# Revit family: Mailboxes_Aluminum-Standard_System-Salsbury_Industries-Wall_Installation
name_source: partatom
category: Specialty Equipment
revit_build: Autodesk Revit 2016 (Build: 20150714_1515(x64)
units: mm (PartAtom-declared; Revit-internal decimal feet)

## family parameters
Always vertical = Yes
Cut with Voids When Loaded = No
Host = Wall
OmniClass Number = 23.40.90.14.11
OmniClass Title = Mail Boxes
Part Type = Normal
Room Calculation Point = No
Round Connector Dimension = Use Diameter
Shared = No

## types (2) — shared parameters
2x4 Platform Support = Softwood, Lumber
2x4 Spacing = 24 "
Assembly Code = C1030910
Back Enclosure Material = Steel - Salsbury Finish - Clear
Base Depth = 16 "
Description = For Rear Loading Unit Installation
Front Panel Material = Aluminum - Salsbury Finish - Aluminum
Lock Material = Stainless Steel -Salsbury Finish - Polished
Manufacturer = Salsbury Industries
MasterFormat Number = 10 55 00
MasterFormat Title = Postal Specialties
Model = Wall Installation for 2200 Series Aluminum Mailboxes
OmniClass 23 Number = 23.40.90.14.11
OmniClass 23 Title = Mail Boxes
Platform Material = Plywood
Right Rough Opening Offset = 1.5 "
Rough Opening Height = 60 "
Rough Opening Width = 22.5 "
Trim Material = Aluminum - Salsbury Finish - Black
Type Comments = 2 Unit High Installation of models 2230, 2220, 2218, 2214, 2210, 2206
URL = www.mailboxes.com
Version = 2.0 (06/31/18)

## per-type parameters (varying)
| type | Add On Column (not applicable) | Installation Type | Left Rough Opening Offset |
| Starter Column - 2200 Series Aluminum Mailboxes-Standard System - 2 Unit High Installation | Yes | Starter Column | 1.5 " |
| Right Side Add On Column - 2200 Series Aluminum Mailboxes-Standard System - 2 Unit High Installation | No | Add On Column | 0 " |

## geometry (parser evidence)
native form markers: Extrusion x1, Sweep x12
no freeform markers — native parametric forms only
